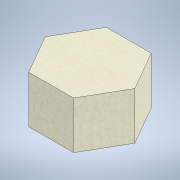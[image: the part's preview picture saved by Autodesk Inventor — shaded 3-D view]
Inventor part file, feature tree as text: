
AUTODESK INVENTOR PART (.ipt)
format: ipt  version: 2021 (Build 250183000, 183)  size: 118,784 bytes
history: native  units: mm
features: extrude x1, sketch x1
ambient origin geometry x8: Origin, YZ Plane, XZ Plane, XY Plane, X Axis, Y Axis, Z Axis, Center Point
bodies: Solid1 (feature_tree)
feature tree (2):
  extrude  "Extrusion1"  Depth=61.6mm TaperAngle=0.0deg
  sketch  "Sketch1"  dims[d0=101.0mm d1=61.6mm d2=0.0mm]
